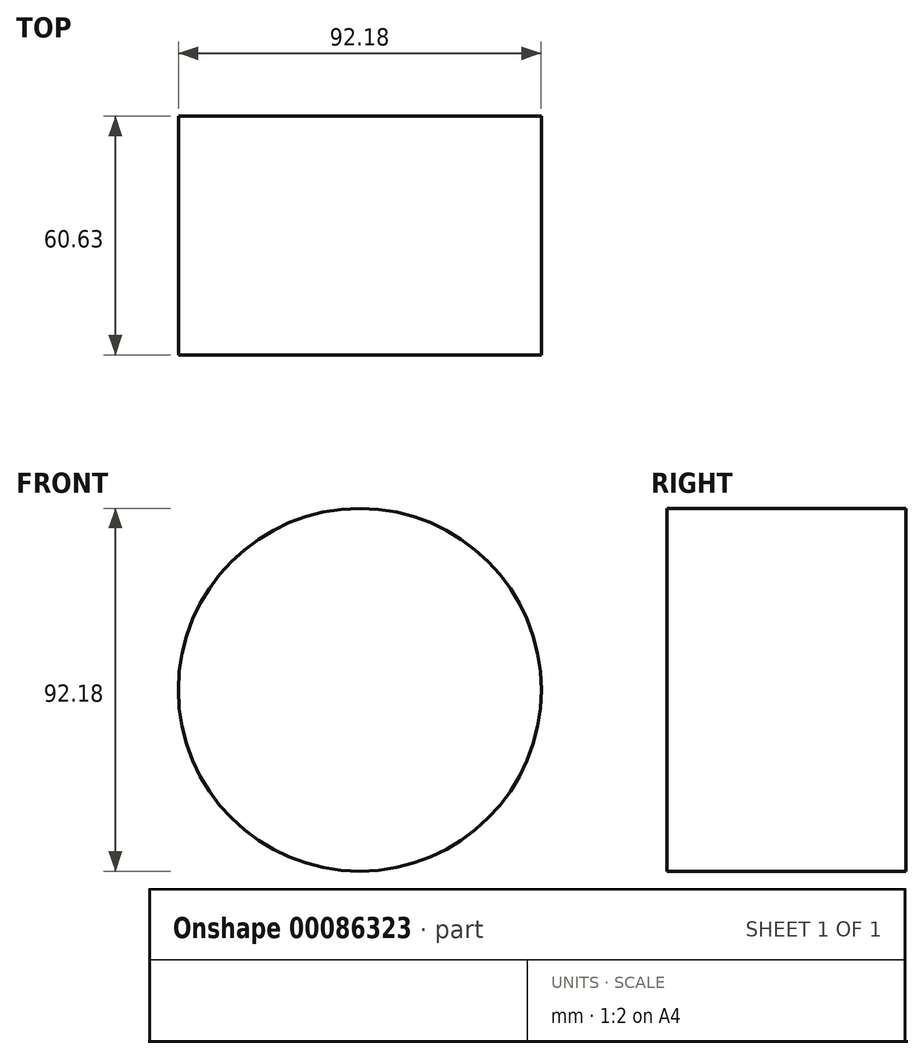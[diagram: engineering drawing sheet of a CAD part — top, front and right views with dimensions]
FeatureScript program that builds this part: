
annotation { "Feature Type Name" : "Feature", "Feature Type Description" : "" }
export const myFeature = defineFeature(function(context is Context, id is Id, definition is map)
    precondition{}
    {
        {
            var Q0;
            Q0=qCreatedBy(makeId("Front.planeOp"),FACE);
            var sketch = newSketch(context, id + "F0", { "sketchPlane" : qUnion([Q0])});
            skCircle(sketch, "E0", {"center": v(0, 0) * mm, "radius": 46.1 * mm});
            skSolve(sketch);
        }
        {
            var Q0;
            Q0=sQuery(id+"F0.wireOp",EDGE,"E0");
            extrude(context, id + "F1", {"bodyType" : ToolBodyType.SURFACE, "surfaceEntities" : qUnion([Q0]), "depth" : 60.63 * mm});
        }
    });
